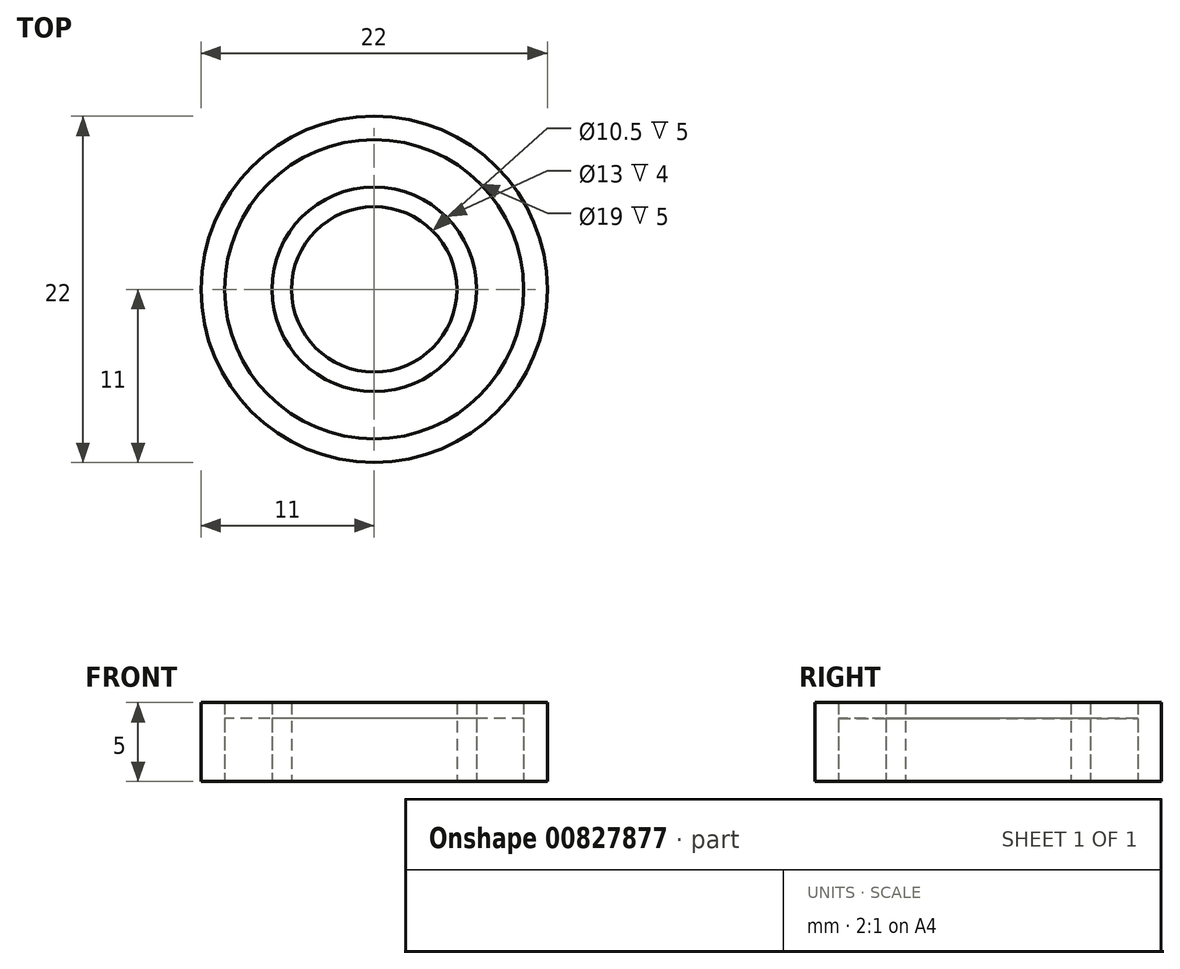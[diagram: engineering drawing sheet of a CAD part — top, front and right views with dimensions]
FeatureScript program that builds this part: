
annotation { "Feature Type Name" : "Feature", "Feature Type Description" : "" }
export const myFeature = defineFeature(function(context is Context, id is Id, definition is map)
    precondition{}
    {
        {
            var Q0;
            Q0=qCreatedBy(makeId("Top.planeOp"),FACE);
            var sketch = newSketch(context, id + "F0", { "sketchPlane" : qUnion([Q0])});
            skCircle(sketch, "E0", {"center": v(0, 0) * mm, "radius": 11 * mm});
            skCircle(sketch, "E1", {"center": v(0, 0) * mm, "radius": 9.5 * mm});
            skCircle(sketch, "E2", {"center": v(0, 0) * mm, "radius": 5.25 * mm});
            skCircle(sketch, "E3", {"center": v(0, 0) * mm, "radius": 6.5 * mm});
            skSolve(sketch);
        }
        {
            var Q0;
            Q0=makeQuery(id+"F0.imprint","IMPRINT",FACE,{"disambiguationData":[TD([[makeQuery(id+"F0.imprint","IMPRINT",EDGE,{"derivedFrom":sQuery(id+"F0.wireOp",EDGE,"E0")}),1.0]])]});
            extrude(context, id + "F1", {"entities" : qUnion([Q0]), "depth" : 5 * mm, "offsetDistance" : 25 * mm});
        }
        {
            var Q0;
            Q0=makeQuery(id+"F0.imprint","IMPRINT",FACE,{"disambiguationData":[TD([[makeQuery(id+"F0.imprint","IMPRINT",EDGE,{"derivedFrom":sQuery(id+"F0.wireOp",EDGE,"E2")}),-1.0]])]});
            extrude(context, id + "F2", {"entities" : qUnion([Q0]), "depth" : 5 * mm, "offsetDistance" : 25 * mm});
        }
        {
            var Q0;
            Q0=makeQuery(id+"F0.imprint","IMPRINT",FACE,{"disambiguationData":[TD([[makeQuery(id+"F0.imprint","IMPRINT",EDGE,{"derivedFrom":sQuery(id+"F0.wireOp",EDGE,"E1")}),1.0]])]});
            extrude(context, id + "F3", {"entities" : qUnion([Q0]), "depth" : 4 * mm, "offsetDistance" : 25 * mm});
        }
    });
